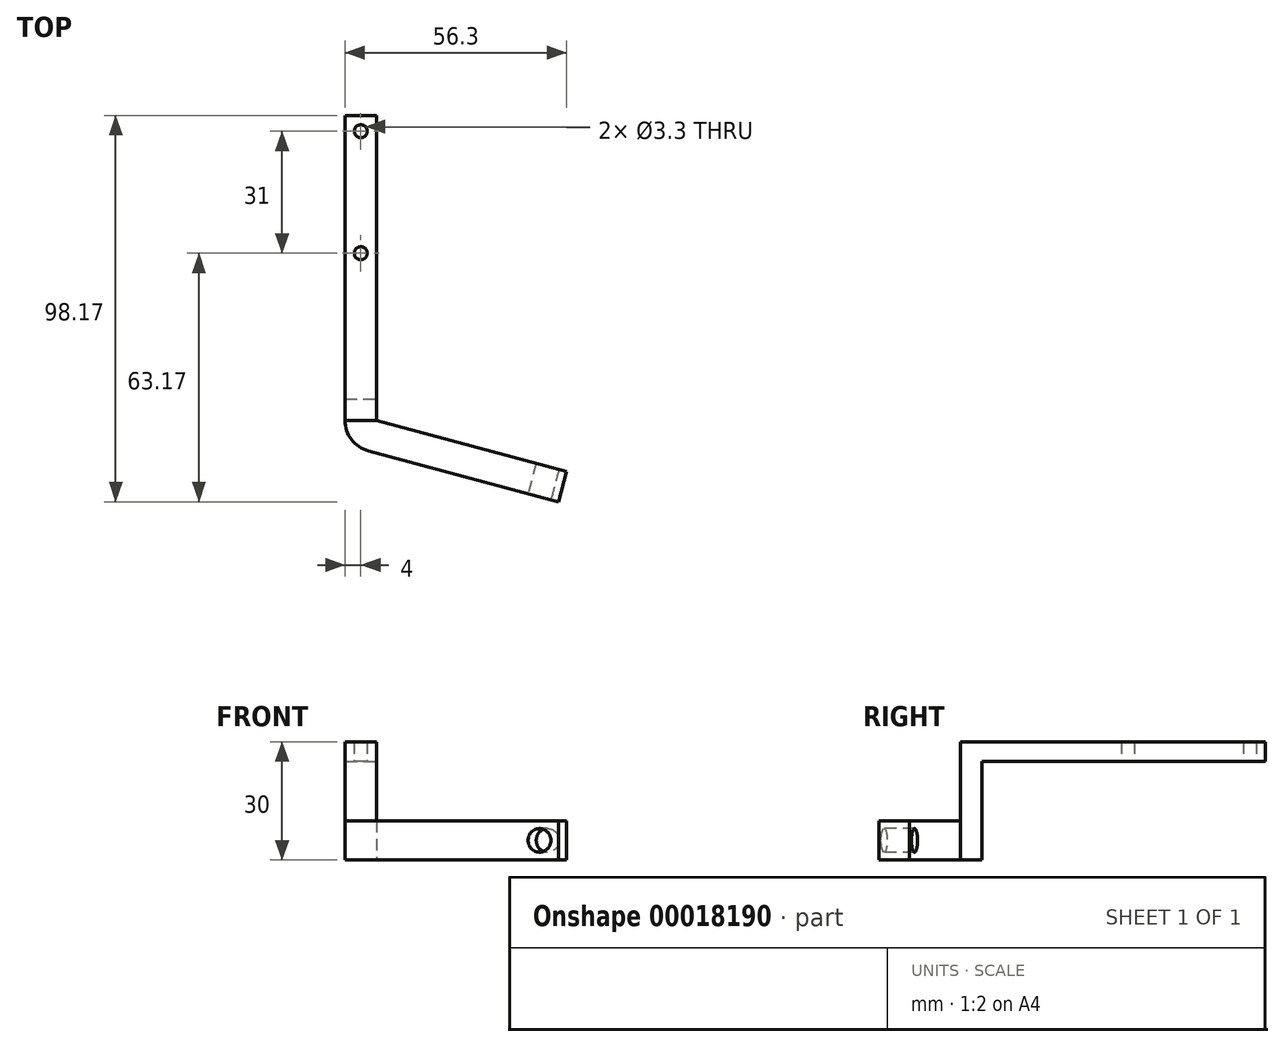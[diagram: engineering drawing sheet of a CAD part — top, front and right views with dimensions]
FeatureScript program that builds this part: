
annotation { "Feature Type Name" : "Feature", "Feature Type Description" : "" }
export const myFeature = defineFeature(function(context is Context, id is Id, definition is map)
    precondition{}
    {
        {
            var Q0;
            Q0=qCreatedBy(makeId("Top.planeOp"),FACE);
            var sketch = newSketch(context, id + "F0", { "sketchPlane" : qUnion([Q0])});
            skLineSegment(sketch, "E0.bottom", {"start": v(-8, 77.5) * mm, "end": v(0, 77.5) * mm});
            skLineSegment(sketch, "E0.top", {"start": v(-8, 0) * mm, "end": v(0, 0) * mm});
            skLineSegment(sketch, "E0.left", {"start": v(-8, 77.5) * mm, "end": v(-8, 0) * mm});
            skLineSegment(sketch, "E0.right", {"start": v(0, 77.5) * mm, "end": v(0, 0) * mm});
            skLineSegment(sketch, "E1", {"start": v(-4, 77.5) * mm, "end": v(-4, 0) * mm, "construction": true});
            skCircle(sketch, "E2", {"center": v(-4, 42.5) * mm, "radius": 1.65 * mm});
            skLineSegment(sketch, "E3.top", {"start": v(-8, 5.5) * mm, "end": v(0, 5.5) * mm});
            skLineSegment(sketch, "E3.left", {"start": v(-8, 0) * mm, "end": v(-8, 5.5) * mm});
            skLineSegment(sketch, "E3.right", {"start": v(0, 0) * mm, "end": v(0, 5.5) * mm});
            skCircle(sketch, "E4", {"center": v(-4, 73.5) * mm, "radius": 1.65 * mm});
            skSolve(sketch);
        }
        {
            var Q0;
            Q0=makeQuery(id+"F0.imprint","IMPRINT",FACE,{"disambiguationData":[TD([[makeQuery(id+"F0.imprint","IMPRINT",EDGE,{"derivedFrom":sQuery(id+"F0.wireOp",EDGE,"E0.bottom")}),-1.0]])]});
            var Q1;
            Q1=makeQuery(id+"F0.imprint","IMPRINT",FACE,{"disambiguationData":[TD([[makeQuery(id+"F0.imprint","IMPRINT",EDGE,{"derivedFrom":sQuery(id+"F0.wireOp",EDGE,"E0.top")}),1.0]])]});
            extrude(context, id + "F1", {"entities" : qUnion([Q0, Q1]), "depth" : 5 * mm});
        }
        {
            var Q0;
            Q0=makeQuery(id+"F0.imprint","IMPRINT",FACE,{"disambiguationData":[TD([[makeQuery(id+"F0.imprint","IMPRINT",EDGE,{"derivedFrom":sQuery(id+"F0.wireOp",EDGE,"E0.top")}),1.0]])]});
            extrude(context, id + "F2", {"entities" : qUnion([Q0]), "operationType" : NewBodyOperationType.ADD, "oppositeDirection" : true, "depth" : 25 * mm});
        }
        {
            var Q0;
            {var subQ0=sQuery(id+"F0.wireOp",EDGE,"E0.top");Q0=makeQuery(id+"F2.boolean.opBoolean","MERGE",FACE,{"derivedFrom":[makeQuery(id+"F1.opExtrude","SWEPT_FACE",FACE,{"disambiguationData":[OSD([subQ0])]}),makeQuery(id+"F2.opExtrude","SWEPT_FACE",FACE,{"disambiguationData":[OSD([subQ0])]})]});}
            var sketch = newSketch(context, id + "F3", { "sketchPlane" : qUnion([Q0])});
            skLineSegment(sketch, "E5.bottom", {"start": v(-8, -25) * mm, "end": v(0, -25) * mm});
            skLineSegment(sketch, "E5.top", {"start": v(-8, -15) * mm, "end": v(0, -15) * mm});
            skLineSegment(sketch, "E5.left", {"start": v(-8, -25) * mm, "end": v(-8, -15) * mm});
            skLineSegment(sketch, "E5.right", {"start": v(0, -25) * mm, "end": v(0, -15) * mm});
            skSolve(sketch);
        }
        {
            var Q0;
            Q0=makeQuery(id+"F3.imprint","IMPRINT",FACE,{"disambiguationData":[TD([[makeQuery(id+"F3.imprint","IMPRINT",EDGE,{"derivedFrom":sQuery(id+"F3.wireOp",EDGE,"E5.bottom")}),1.0]])]});
            var Q1;
            Q1=sQuery(id+"F3.wireOp",EDGE,"E5.right");
            revolve(context, id + "F4", {"operationType" : NewBodyOperationType.ADD, "entities" : qUnion([Q0]), "axis" : qUnion([Q1]), "revolveType" : RevolveType.ONE_DIRECTION, "angle" : 75 * degree});
        }
        {
            var Q0;
            Q0=makeQuery(id+"F4.opRevolve","CAP_FACE",FACE,{"disambiguationData":[OSD([sQuery(id+"F3.wireOp",EDGE,"E5.bottom"),sQuery(id+"F3.wireOp",EDGE,"E5.top"),sQuery(id+"F3.wireOp",EDGE,"E5.left"),sQuery(id+"F3.wireOp",EDGE,"E5.right")])],"isStart":false});
            extrude(context, id + "F5", {"entities" : qUnion([Q0]), "operationType" : NewBodyOperationType.ADD, "depth" : 50 * mm});
        }
        {
            var Q0;
            Q0=makeQuery(id+"F5.opExtrude","SWEPT_FACE",FACE,{"disambiguationData":[OSD([sQuery(id+"F3.wireOp",EDGE,"E5.left")])]});
            var sketch = newSketch(context, id + "F6", { "sketchPlane" : qUnion([Q0])});
            skLineSegment(sketch, "E6", {"start": v(0, -20) * mm, "end": v(50, -20) * mm, "construction": true});
            skPoint(sketch, "E7", {"position": v(45, -20) * mm});
            skSolve(sketch);
        }
        {
            var Q0;
            Q0=sQuery(id+"F6.wireOp",VERTEX,"E7");
            var Q1;
            Q1=makeQuery(id+"F1.opExtrude","SWEPT_BODY",BODY,{"disambiguationData":[OSD([sQuery(id+"F0.wireOp",EDGE,"E0.bottom"),sQuery(id+"F0.wireOp",EDGE,"E0.left"),sQuery(id+"F0.wireOp",EDGE,"E0.right"),sQuery(id+"F0.wireOp",EDGE,"E2"),sQuery(id+"F0.wireOp",EDGE,"8a2cc71e-c3be-4ba8-a8b7-0444bd9d71a8"),sQuery(id+"F0.wireOp",EDGE,"E0.top"),sQuery(id+"F0.wireOp",EDGE,"E3.left"),sQuery(id+"F0.wireOp",EDGE,"E3.right")])]});
            hole(context, id + "F7", {"style" : HoleStyle.SIMPLE, "holeDiameter" : 6 * mm, "endStyle" : HoleEndStyle.THROUGH, "locations" : qUnion([Q0]), "scope" : qUnion([Q1])});
        }
    });
